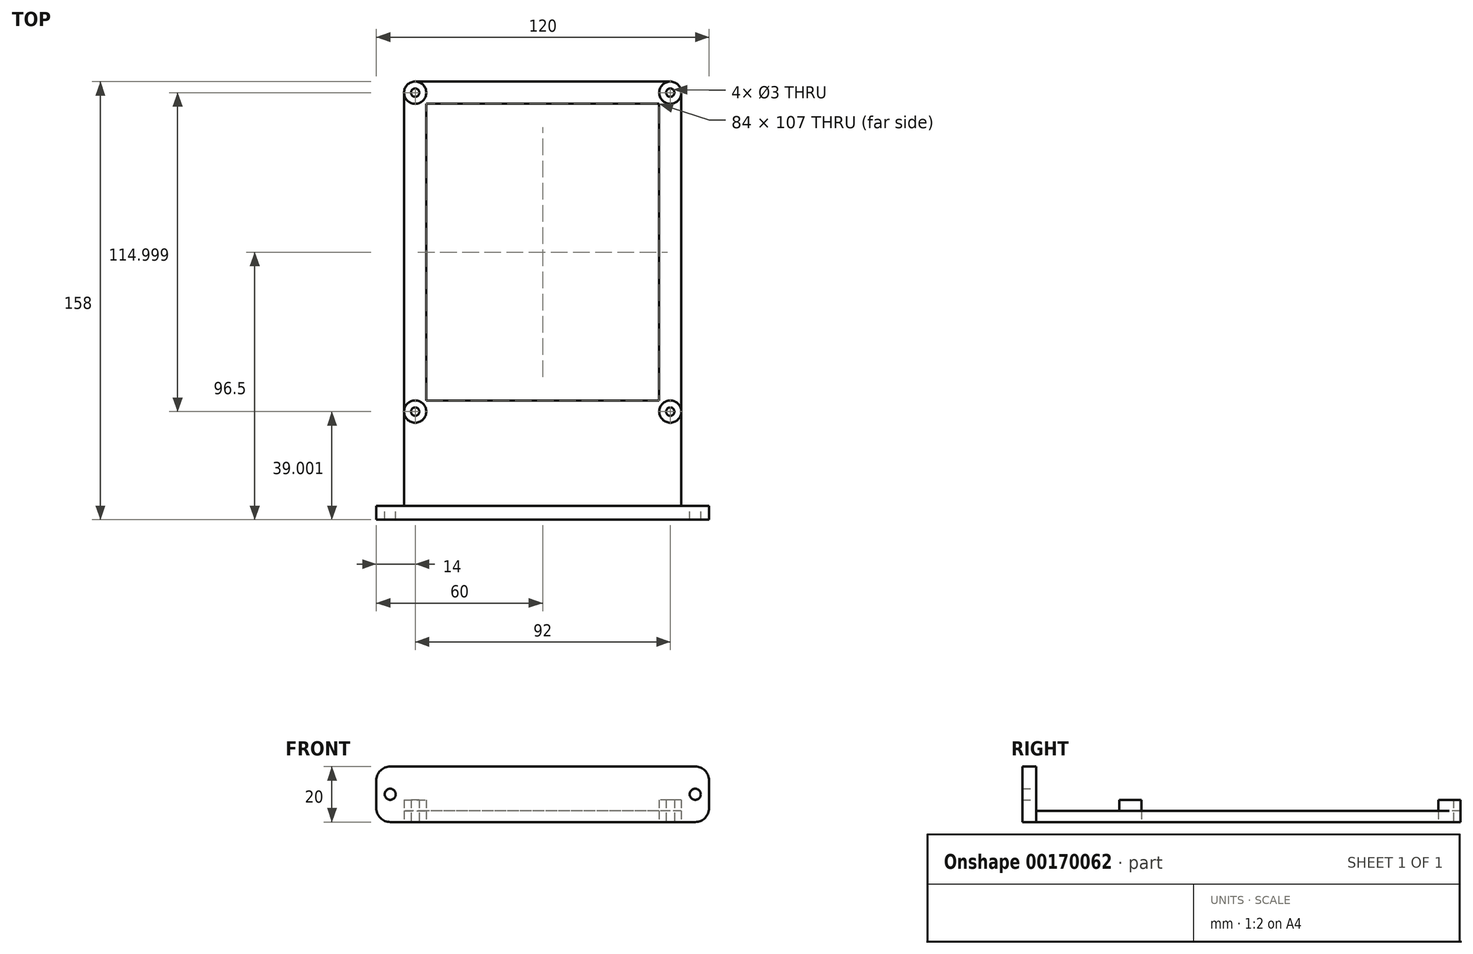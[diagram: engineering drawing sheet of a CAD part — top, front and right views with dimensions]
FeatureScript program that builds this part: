
annotation { "Feature Type Name" : "Feature", "Feature Type Description" : "" }
export const myFeature = defineFeature(function(context is Context, id is Id, definition is map)
    precondition{}
    {
        {
            var Q0;
            Q0=qCreatedBy(makeId("Top.planeOp"),FACE);
            var sketch = newSketch(context, id + "F0", { "sketchPlane" : qUnion([Q0])});
            skLineSegment(sketch, "E0.bottom", {"start": v(50, -61.5) * mm, "end": v(-50, -61.5) * mm});
            skLineSegment(sketch, "E0.top", {"start": v(50, 61.5) * mm, "end": v(-50, 61.5) * mm});
            skLineSegment(sketch, "E0.left", {"start": v(50, -61.5) * mm, "end": v(50, 61.5) * mm});
            skLineSegment(sketch, "E0.right", {"start": v(-50, -61.5) * mm, "end": v(-50, 61.5) * mm});
            skPoint(sketch, "E0.middle", {"position": v(0, 0) * mm});
            skCircle(sketch, "E1", {"center": v(-46, 57.5) * mm, "radius": 1.5 * mm});
            skCircle(sketch, "E2", {"center": v(46, 57.5) * mm, "radius": 1.5 * mm});
            skCircle(sketch, "E3", {"center": v(46, -57.5) * mm, "radius": 1.5 * mm});
            skCircle(sketch, "E4", {"center": v(-46, -57.5) * mm, "radius": 1.5 * mm});
            skLineSegment(sketch, "E5.bottom", {"start": v(42, 53.5) * mm, "end": v(-42, 53.5) * mm});
            skLineSegment(sketch, "E5.top", {"start": v(42, -53.5) * mm, "end": v(-42, -53.5) * mm});
            skLineSegment(sketch, "E5.left", {"start": v(42, 53.5) * mm, "end": v(42, -53.5) * mm});
            skLineSegment(sketch, "E5.right", {"start": v(-42, 53.5) * mm, "end": v(-42, -53.5) * mm});
            skSolve(sketch);
        }
        {
            var Q0;
            Q0=makeQuery(id+"F0.imprint","IMPRINT",FACE,{"disambiguationData":[TD([[makeQuery(id+"F0.imprint","IMPRINT",EDGE,{"derivedFrom":sQuery(id+"F0.wireOp",EDGE,"E0.bottom")}),-1.0]])]});
            extrude(context, id + "F1", {"entities" : qUnion([Q0]), "depth" : 4 * mm});
        }
        {
            var Q0;
            Q0=makeQuery(id+"F1.opExtrude","CAP_FACE",FACE,{"disambiguationData":[OSD([sQuery(id+"F0.wireOp",EDGE,"E0.bottom"),sQuery(id+"F0.wireOp",EDGE,"E0.top"),sQuery(id+"F0.wireOp",EDGE,"E0.left"),sQuery(id+"F0.wireOp",EDGE,"E0.right"),sQuery(id+"F0.wireOp",EDGE,"E1"),sQuery(id+"F0.wireOp",EDGE,"E2"),sQuery(id+"F0.wireOp",EDGE,"E3"),sQuery(id+"F0.wireOp",EDGE,"E4"),sQuery(id+"F0.wireOp",EDGE,"E5.bottom"),sQuery(id+"F0.wireOp",EDGE,"E5.top"),sQuery(id+"F0.wireOp",EDGE,"E5.left"),sQuery(id+"F0.wireOp",EDGE,"E5.right")])],"isStart":false});
            var sketch = newSketch(context, id + "F2", { "sketchPlane" : qUnion([Q0])});
            skCircle(sketch, "E6", {"center": v(46, -57.5) * mm, "radius": 4 * mm});
            skCircle(sketch, "E7", {"center": v(-46, -57.5) * mm, "radius": 4 * mm});
            skCircle(sketch, "E8", {"center": v(-46, 57.5) * mm, "radius": 4 * mm});
            skCircle(sketch, "E9", {"center": v(46, 57.5) * mm, "radius": 4 * mm});
            skSolve(sketch);
        }
        {
            var Q0;
            Q0=makeQuery(id+"F2.imprint","IMPRINT",FACE,{"disambiguationData":[TD([[makeQuery(id+"F2.imprint","IMPRINT",EDGE,{"derivedFrom":makeQuery(id+"F1.opExtrude","CAP_EDGE",EDGE,{"disambiguationData":[OSD([sQuery(id+"F0.wireOp",EDGE,"E1")])],"isStart":false})}),-1.0]])]});
            var Q1;
            Q1=makeQuery(id+"F2.imprint","IMPRINT",FACE,{"disambiguationData":[TD([[makeQuery(id+"F2.imprint","IMPRINT",EDGE,{"derivedFrom":makeQuery(id+"F1.opExtrude","CAP_EDGE",EDGE,{"disambiguationData":[OSD([sQuery(id+"F0.wireOp",EDGE,"E2")])],"isStart":false})}),-1.0]])]});
            var Q2;
            Q2=makeQuery(id+"F2.imprint","IMPRINT",FACE,{"disambiguationData":[TD([[makeQuery(id+"F2.imprint","IMPRINT",EDGE,{"derivedFrom":makeQuery(id+"F1.opExtrude","CAP_EDGE",EDGE,{"disambiguationData":[OSD([sQuery(id+"F0.wireOp",EDGE,"E3")])],"isStart":false})}),-1.0]])]});
            var Q3;
            Q3=makeQuery(id+"F2.imprint","IMPRINT",FACE,{"disambiguationData":[TD([[makeQuery(id+"F2.imprint","IMPRINT",EDGE,{"derivedFrom":makeQuery(id+"F1.opExtrude","CAP_EDGE",EDGE,{"disambiguationData":[OSD([sQuery(id+"F0.wireOp",EDGE,"E4")])],"isStart":false})}),-1.0]])]});
            extrude(context, id + "F3", {"entities" : qUnion([Q0, Q1, Q2, Q3]), "operationType" : NewBodyOperationType.ADD, "depth" : 4 * mm});
        }
        {
            var Q0;
            Q0=makeQuery(id+"F1.opExtrude","SWEPT_FACE",FACE,{"disambiguationData":[OSD([sQuery(id+"F0.wireOp",EDGE,"E0.bottom")])]});
            var sketch = newSketch(context, id + "F4", { "sketchPlane" : qUnion([Q0])});
            skLineSegment(sketch, "E10.bottom", {"start": v(-50, 4) * mm, "end": v(50, 4) * mm});
            skLineSegment(sketch, "E10.top", {"start": v(-50, 0) * mm, "end": v(50, 0) * mm});
            skLineSegment(sketch, "E10.left", {"start": v(-50, 4) * mm, "end": v(-50, 0) * mm});
            skLineSegment(sketch, "E10.right", {"start": v(50, 4) * mm, "end": v(50, 0) * mm});
            skSolve(sketch);
        }
        {
            var Q0;
            Q0 = qSketchRegion(id + "F4", true);
            extrude(context, id + "F5", {"entities" : qUnion([Q0]), "operationType" : NewBodyOperationType.ADD, "depth" : 30 * mm});
        }
        {
            var Q0;
            Q0=makeQuery(id+"F5.boolean.opBoolean","MERGE",FACE,{"derivedFrom":[makeQuery(id+"F1.opExtrude","CAP_FACE",FACE,{"disambiguationData":[OSD([sQuery(id+"F0.wireOp",EDGE,"E0.bottom"),sQuery(id+"F0.wireOp",EDGE,"E0.top"),sQuery(id+"F0.wireOp",EDGE,"E0.left"),sQuery(id+"F0.wireOp",EDGE,"E0.right"),sQuery(id+"F0.wireOp",EDGE,"E1"),sQuery(id+"F0.wireOp",EDGE,"E2"),sQuery(id+"F0.wireOp",EDGE,"E3"),sQuery(id+"F0.wireOp",EDGE,"E4"),sQuery(id+"F0.wireOp",EDGE,"E5.bottom"),sQuery(id+"F0.wireOp",EDGE,"E5.top"),sQuery(id+"F0.wireOp",EDGE,"E5.left"),sQuery(id+"F0.wireOp",EDGE,"E5.right")])],"isStart":true}),makeQuery(id+"F5.opExtrude","SWEPT_FACE",FACE,{"disambiguationData":[OSD([sQuery(id+"F4.wireOp",EDGE,"E10.top")])]})]});
            var sketch = newSketch(context, id + "F6", { "sketchPlane" : qUnion([Q0])});
            skLineSegment(sketch, "E11.bottom", {"start": v(60, 91.5) * mm, "end": v(-50, 91.5) * mm});
            skLineSegment(sketch, "E11.top", {"start": v(60, 96.5) * mm, "end": v(-50, 96.5) * mm});
            skLineSegment(sketch, "E11.right", {"start": v(60, 91.5) * mm, "end": v(60, 96.5) * mm});
            skLineSegment(sketch, "E12.bottom", {"start": v(-50, 96.5) * mm, "end": v(-60, 96.5) * mm});
            skLineSegment(sketch, "E12.top", {"start": v(-50, 91.5) * mm, "end": v(-60, 91.5) * mm});
            skLineSegment(sketch, "E12.right", {"start": v(-60, 96.5) * mm, "end": v(-60, 91.5) * mm});
            skSolve(sketch);
        }
        {
            var Q0;
            Q0=makeQuery(id+"F6.imprint","IMPRINT",FACE,{"disambiguationData":[TD([[makeQuery(id+"F6.imprint","IMPRINT",EDGE,{"derivedFrom":sQuery(id+"F6.wireOp",EDGE,"E11.top")}),1.0]])]});
            extrude(context, id + "F7", {"entities" : qUnion([Q0]), "operationType" : NewBodyOperationType.ADD, "oppositeDirection" : true, "depth" : 20 * mm});
        }
        {
            var Q0;
            Q0=makeQuery(id+"F7.opExtrude","CAP_EDGE",EDGE,{"disambiguationData":[OSD([sQuery(id+"F6.wireOp",EDGE,"E12.right")])],"isStart":false});
            var Q1;
            Q1=makeQuery(id+"F7.opExtrude","CAP_EDGE",EDGE,{"disambiguationData":[OSD([sQuery(id+"F6.wireOp",EDGE,"E12.right")])],"isStart":true});
            var Q2;
            Q2=makeQuery(id+"F7.opExtrude","CAP_EDGE",EDGE,{"disambiguationData":[OSD([sQuery(id+"F6.wireOp",EDGE,"E11.right")])],"isStart":true});
            var Q3;
            Q3=makeQuery(id+"F7.opExtrude","CAP_EDGE",EDGE,{"disambiguationData":[OSD([sQuery(id+"F6.wireOp",EDGE,"E11.right")])],"isStart":false});
            var Q4;
            Q4=makeQuery(id+"F5.opExtrude","CAP_EDGE",EDGE,{"disambiguationData":[OSD([sQuery(id+"F4.wireOp",EDGE,"E10.right")])],"isStart":false});
            var Q5;
            Q5=makeQuery(id+"F5.opExtrude","CAP_EDGE",EDGE,{"disambiguationData":[OSD([sQuery(id+"F4.wireOp",EDGE,"E10.left")])],"isStart":false});
            fillet(context, id + "F8", {"entities" : qUnion([Q0, Q1, Q2, Q3, Q4, Q5]), "radius" : 5 * mm, "tangentPropagation" : true, "allowEdgeOverflow" : false});
        }
        {
            var Q0;
            Q0=makeQuery(id+"F1.opExtrude","SWEPT_EDGE",EDGE,{"disambiguationData":[OSD([sQuery(id+"F0.wireOp",EDGE,"E0.top"),sQuery(id+"F0.wireOp",EDGE,"E0.left")])]});
            var Q1;
            Q1=makeQuery(id+"F1.opExtrude","SWEPT_EDGE",EDGE,{"disambiguationData":[OSD([sQuery(id+"F0.wireOp",EDGE,"E0.top"),sQuery(id+"F0.wireOp",EDGE,"E0.right")])]});
            fillet(context, id + "F9", {"entities" : qUnion([Q0, Q1]), "radius" : 4 * mm, "tangentPropagation" : true, "allowEdgeOverflow" : false});
        }
        {
            var Q0;
            Q0=makeQuery(id+"F7.opExtrude","SWEPT_FACE",FACE,{"disambiguationData":[OSD([sQuery(id+"F6.wireOp",EDGE,"E11.bottom"),sQuery(id+"F6.wireOp",EDGE,"E12.top")])]});
            var sketch = newSketch(context, id + "F10", { "sketchPlane" : qUnion([Q0])});
            skCircle(sketch, "E13", {"center": v(55, 10) * mm, "radius": 2 * mm});
            skPoint(sketch, "E13.centerSnap0", {"position": v(60, 10) * mm});
            skCircle(sketch, "E14", {"center": v(-55, 10) * mm, "radius": 2 * mm});
            skPoint(sketch, "E14.centerSnap0", {"position": v(-60, 10) * mm});
            skSolve(sketch);
        }
        {
            var Q0;
            Q0=makeQuery(id+"F10.imprint","IMPRINT",FACE,{"disambiguationData":[TD([[makeQuery(id+"F10.imprint","IMPRINT",EDGE,{"derivedFrom":sQuery(id+"F10.wireOp",EDGE,"E13")}),1.0]])]});
            var Q1;
            Q1=makeQuery(id+"F10.imprint","IMPRINT",FACE,{"disambiguationData":[TD([[makeQuery(id+"F10.imprint","IMPRINT",EDGE,{"derivedFrom":sQuery(id+"F10.wireOp",EDGE,"E14")}),1.0]])]});
            extrude(context, id + "F11", {"entities" : qUnion([Q0, Q1]), "operationType" : NewBodyOperationType.REMOVE, "oppositeDirection" : true, "depth" : 10 * mm});
        }
    });
